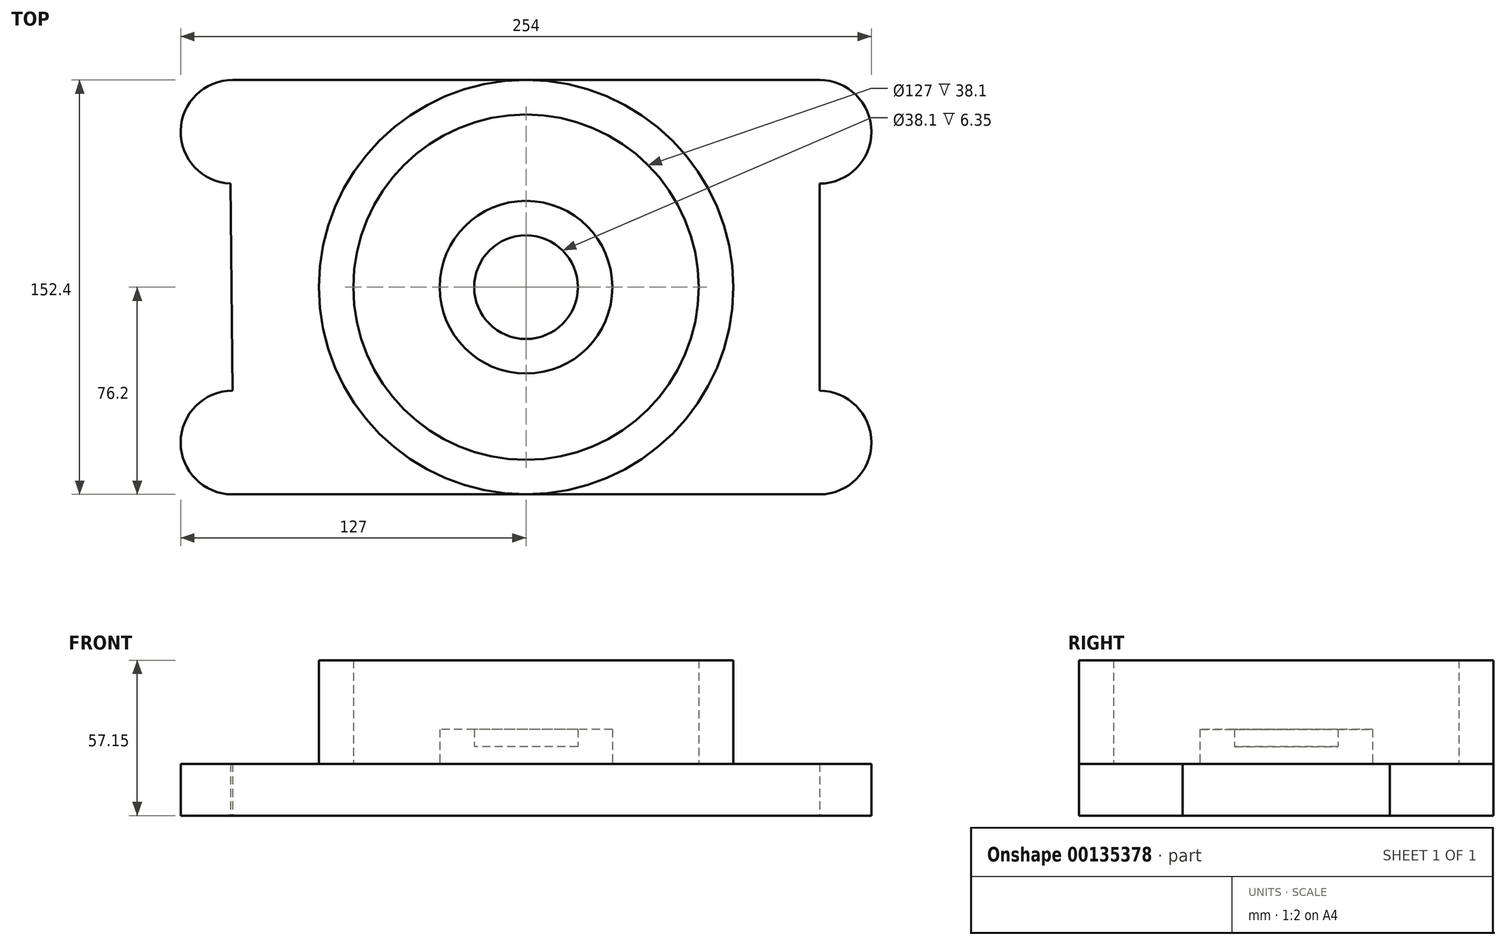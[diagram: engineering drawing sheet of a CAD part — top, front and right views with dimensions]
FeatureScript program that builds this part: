
annotation { "Feature Type Name" : "Feature", "Feature Type Description" : "" }
export const myFeature = defineFeature(function(context is Context, id is Id, definition is map)
    precondition{}
    {
        {
            var Q0;
            Q0=qCreatedBy(makeId("Top.planeOp"),FACE);
            var sketch = newSketch(context, id + "F0", { "sketchPlane" : qUnion([Q0])});
            skCircle(sketch, "E0", {"center": v(0, 0) * mm, "radius": 19.05 * mm});
            skCircle(sketch, "E1", {"center": v(0, 0) * mm, "radius": 63.5 * mm});
            skCircle(sketch, "E2", {"center": v(0, 0) * mm, "radius": 76.2 * mm});
            skCircle(sketch, "E3", {"center": v(0, 0) * mm, "radius": 31.75 * mm});
            skLineSegment(sketch, "E4", {"start": v(0, 76.2) * mm, "end": v(-107.95, 76.2) * mm});
            skLineSegment(sketch, "E5", {"start": v(0, 76.2) * mm, "end": v(107.95, 76.2) * mm});
            skLineSegment(sketch, "E6", {"start": v(0, -76.2) * mm, "end": v(107.95, -76.2) * mm});
            skLineSegment(sketch, "E7", {"start": v(0, -76.2) * mm, "end": v(-107.95, -76.2) * mm});
            skArc(sketch, "E8", {"start": v(-107.95, 76.2) * mm, "mid": v(-127, 57.54) * mm, "end": v(-108.73, 38.12) * mm});
            skArc(sketch, "E9", {"start": v(-107.95, -38.1) * mm, "mid": v(-127, -57.15) * mm, "end": v(-107.95, -76.2) * mm});
            skLineSegment(sketch, "E10", {"start": v(-108.73, 38.12) * mm, "end": v(-107.95, -38.1) * mm});
            skArc(sketch, "E11", {"start": v(107.95, 38.1) * mm, "mid": v(127, 57.15) * mm, "end": v(107.95, 76.2) * mm});
            skArc(sketch, "E12", {"start": v(107.95, -76.2) * mm, "mid": v(127, -57.15) * mm, "end": v(107.95, -38.1) * mm});
            skLineSegment(sketch, "E13", {"start": v(107.95, 38.1) * mm, "end": v(107.95, -38.1) * mm});
            skSolve(sketch);
        }
        {
            var Q0;
            {var subQ1=sQuery(id+"F0.wireOp",EDGE,"E5");Q0=makeQuery(id+"F0.imprint","IMPRINT",FACE,{"disambiguationData":[TD([[makeQuery(id+"F0.imprint","IMPRINT",EDGE,{"derivedFrom":subQ1}),-1.0]])]});}
            var Q1;
            {var subQ0=sQuery(id+"F0.wireOp",EDGE,"E4");Q1=makeQuery(id+"F0.imprint","IMPRINT",FACE,{"disambiguationData":[TD([[makeQuery(id+"F0.imprint","IMPRINT",EDGE,{"derivedFrom":subQ0}),1.0]])]});}
            var Q2;
            Q2=makeQuery(id+"F0.imprint","IMPRINT",FACE,{"disambiguationData":[TD([[makeQuery(id+"F0.imprint","IMPRINT",EDGE,{"derivedFrom":sQuery(id+"F0.wireOp",EDGE,"E1")}),-1.0]])]});
            var Q3;
            Q3=makeQuery(id+"F0.imprint","IMPRINT",FACE,{"disambiguationData":[TD([[makeQuery(id+"F0.imprint","IMPRINT",EDGE,{"derivedFrom":sQuery(id+"F0.wireOp",EDGE,"E1")}),1.0]])]});
            var Q4;
            Q4=makeQuery(id+"F0.imprint","IMPRINT",FACE,{"disambiguationData":[TD([[makeQuery(id+"F0.imprint","IMPRINT",EDGE,{"derivedFrom":sQuery(id+"F0.wireOp",EDGE,"E0")}),-1.0]])]});
            var Q5;
            Q5=makeQuery(id+"F0.imprint","IMPRINT",FACE,{"disambiguationData":[TD([[makeQuery(id+"F0.imprint","IMPRINT",EDGE,{"derivedFrom":sQuery(id+"F0.wireOp",EDGE,"E0")}),1.0]])]});
            extrude(context, id + "F1", {"entities" : qUnion([Q0, Q1, Q2, Q3, Q4, Q5]), "depth" : 19.05 * mm});
        }
        {
            var Q0;
            Q0=makeQuery(id+"F0.imprint","IMPRINT",FACE,{"disambiguationData":[TD([[makeQuery(id+"F0.imprint","IMPRINT",EDGE,{"derivedFrom":sQuery(id+"F0.wireOp",EDGE,"E1")}),-1.0]])]});
            extrude(context, id + "F2", {"entities" : qUnion([Q0]), "operationType" : NewBodyOperationType.ADD, "depth" : 57.15 * mm});
        }
        {
            var Q0;
            Q0=makeQuery(id+"F0.imprint","IMPRINT",FACE,{"disambiguationData":[TD([[makeQuery(id+"F0.imprint","IMPRINT",EDGE,{"derivedFrom":sQuery(id+"F0.wireOp",EDGE,"E0")}),-1.0]])]});
            extrude(context, id + "F3", {"entities" : qUnion([Q0]), "operationType" : NewBodyOperationType.ADD, "depth" : 31.75 * mm});
        }
        {
            var Q0;
            Q0=makeQuery(id+"F0.imprint","IMPRINT",FACE,{"disambiguationData":[TD([[makeQuery(id+"F0.imprint","IMPRINT",EDGE,{"derivedFrom":sQuery(id+"F0.wireOp",EDGE,"E0")}),1.0]])]});
            extrude(context, id + "F4", {"entities" : qUnion([Q0]), "operationType" : NewBodyOperationType.ADD, "depth" : 25.4 * mm});
        }
    });
